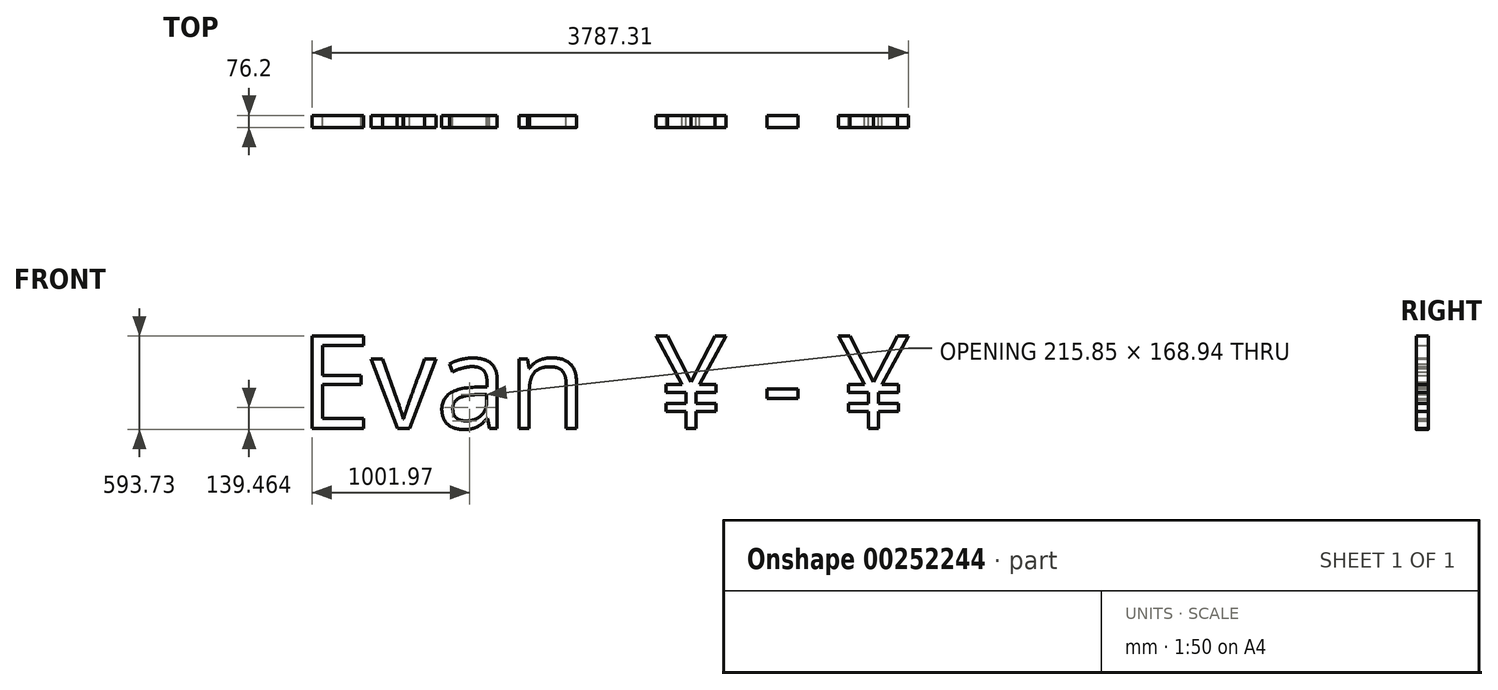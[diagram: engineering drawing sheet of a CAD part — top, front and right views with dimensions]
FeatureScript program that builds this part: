
annotation { "Feature Type Name" : "Feature", "Feature Type Description" : "" }
export const myFeature = defineFeature(function(context is Context, id is Id, definition is map)
    precondition{}
    {
        {
            var Q0;
            Q0=qCreatedBy(makeId("Front.planeOp"),FACE);
            var sketch = newSketch(context, id + "F0", { "sketchPlane" : qUnion([Q0])});
            skText(sketch, "E0", { "text": "Evan  ¥ - ¥", "fontName": "OpenSans-Regular.ttf"});
            const initialGuessF0  = {"E0": [-0.69243, -0.29647, 1, 0, 0.59065]};
            skSetInitialGuess(sketch, initialGuessF0);
            skSolve(sketch);
        }
        {
            var Q0;
            Q0 = qSketchRegion(id + "F0", true);
            extrude(context, id + "F1", {"entities" : qUnion([Q0]), "depth" : 76.2 * mm});
        }
    });
